# Revit family: C250.RFA
name_source: partatom
category: Generic Models
revit_build: Autodesk Revit MEP 2013 (Build: 20130531_2115(x64)
units: mm (PartAtom-declared; Revit-internal decimal feet)

## types (1)
- C2/50  Point-of-use Water Heater
    Backflow Prevention Valve = Not Supplied
    Base Unit Finish = White plastic
    Button Interface = No
    Cable Length and size (If Fitted) = Not Fitted
    Capacity = 5.5 litres
    Control Thermostat Range = 35°C to 75°C
    Enclosure Rating = IP24
    External Material = Impact resiostant Plastic
    Gross Weight (Full) = 8.5kg
    Heat Up Time ((10°C to 65°C) = 10 mins
    Insulation Material = Expanded Polystyrene
    Internal Filter (if fitted) = Not Fitted
    Mains Pressure Limiting Valve = Not Supplied
    Mains Water Connection = 1/2" BSP
    Mains Water Pressure _ Maximum = 0.35MPa (3.5 bar)
    Manufacturer = Zip Industries(UK) Ltd
    Max. Stored Water Temperature = 75°C
    Model = C2/50
    Net Weight (empty) = 3.5kg
    Overall Height = 390
    Overall Length/Depth = 265
    Overall Width = 255
    Power Rating = 2kW
    Power Supply (Voltage) = 230 (v~)
    Product Range = Wall Mounted
    Shape = Rectangular
    Shipping Weight = Not Known
    Standby Power Loss (idle mode) = Not Known
    Supply Phase = 1
    Tank Construction Material = Plastic
    Tap Finish = Chrome
    Type = Point-of-use Water Heater
    Type Comments = Point of use hot water
    URL = www.zipindustries.co.uk
    Unit Access Clearance Bottom = 270mm
    WRAS Approved = Yes
    Warranty ID = 12 months

## geometry (parser evidence)
native form markers: Sweep x3
no freeform markers — native parametric forms only
